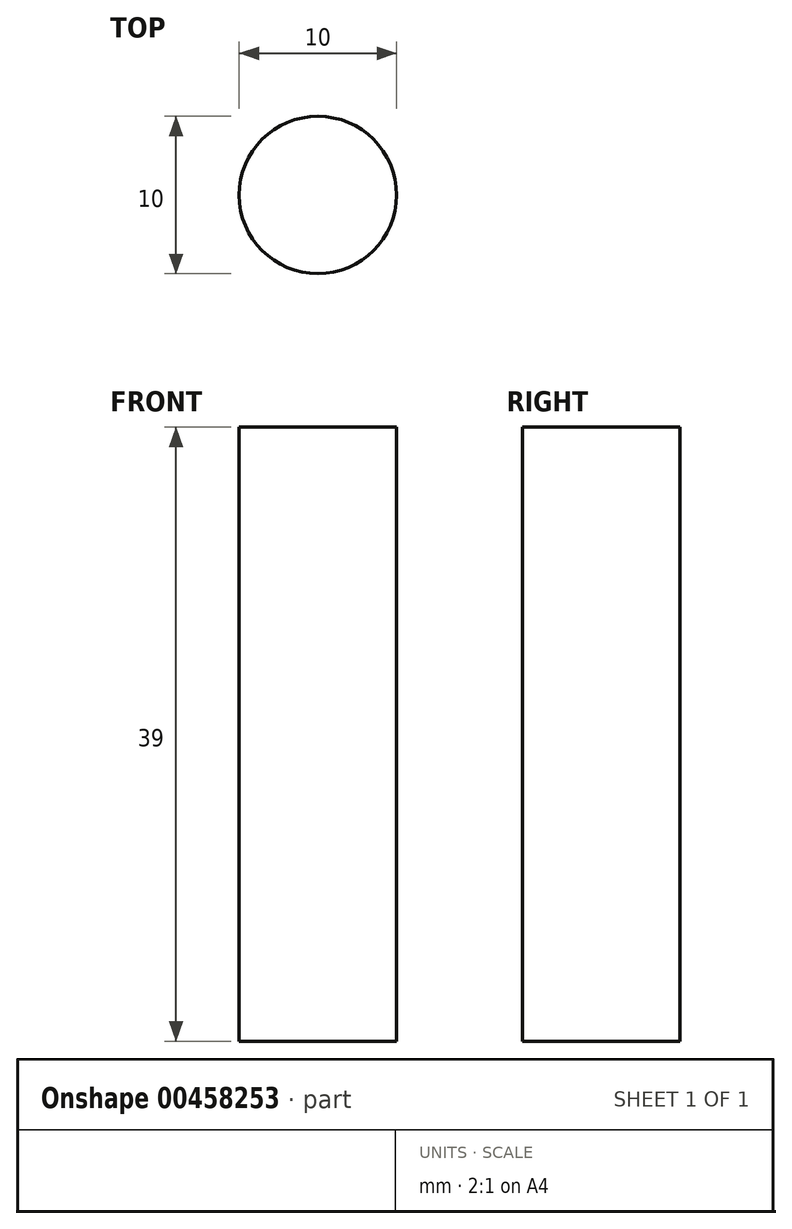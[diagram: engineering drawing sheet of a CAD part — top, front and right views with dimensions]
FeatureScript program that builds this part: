
annotation { "Feature Type Name" : "Feature", "Feature Type Description" : "" }
export const myFeature = defineFeature(function(context is Context, id is Id, definition is map)
    precondition{}
    {
        {
            var Q0;
            Q0=qCreatedBy(makeId("Top.planeOp"),FACE);
            var sketch = newSketch(context, id + "F0", { "sketchPlane" : qUnion([Q0])});
            skCircle(sketch, "E0", {"center": v(0, 0) * mm, "radius": 5 * mm});
            skSolve(sketch);
        }
        {
            var Q0;
            Q0 = qSketchRegion(id + "F0", true);
            extrude(context, id + "F1", {"entities" : qUnion([Q0]), "depth" : 39 * mm, "offsetDistance" : 25 * mm});
        }
    });
